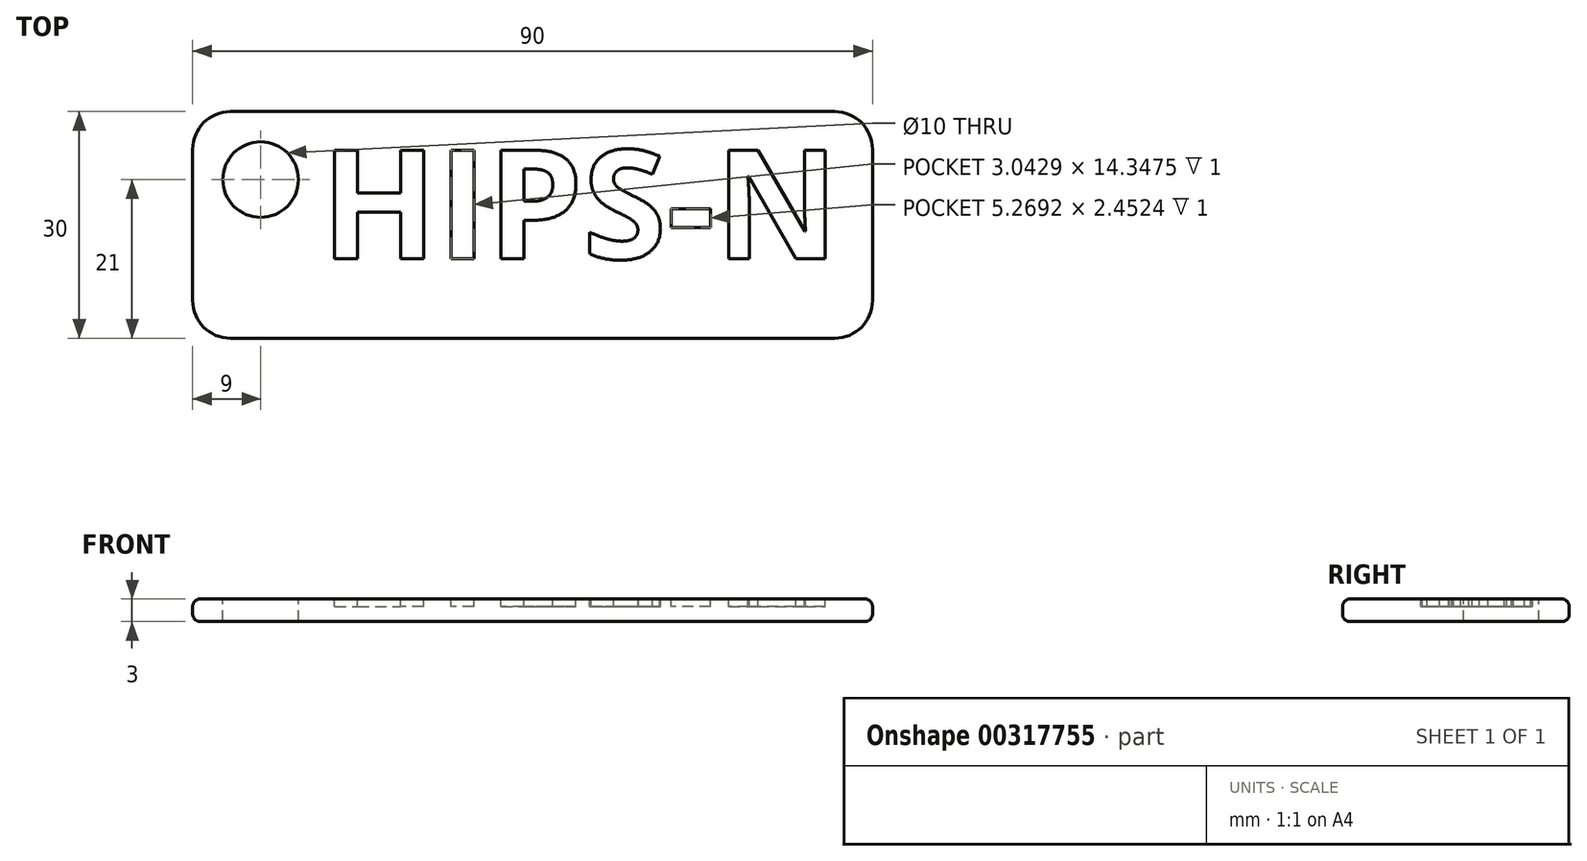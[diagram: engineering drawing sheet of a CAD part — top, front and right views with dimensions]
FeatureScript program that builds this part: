
annotation { "Feature Type Name" : "Feature", "Feature Type Description" : "" }
export const myFeature = defineFeature(function(context is Context, id is Id, definition is map)
    precondition{}
    {
        {
            var Q0;
            Q0=qCreatedBy(makeId("Top.planeOp"),FACE);
            var sketch = newSketch(context, id + "F0", { "sketchPlane" : qUnion([Q0])});
            skLineSegment(sketch, "E0.bottom", {"start": v(-45, 15) * mm, "end": v(45, 15) * mm});
            skLineSegment(sketch, "E0.top", {"start": v(-45, -15) * mm, "end": v(45, -15) * mm});
            skLineSegment(sketch, "E0.left", {"start": v(-45, 15) * mm, "end": v(-45, -15) * mm});
            skLineSegment(sketch, "E0.right", {"start": v(45, 15) * mm, "end": v(45, -15) * mm});
            skLineSegment(sketch, "E1", {"start": v(-45, 15) * mm, "end": v(45, -15) * mm, "construction": true});
            skSolve(sketch);
        }
        {
            var Q0;
            Q0=makeQuery(id+"F0.imprint","IMPRINT",FACE,{"disambiguationData":[TD([[makeQuery(id+"F0.imprint","IMPRINT",EDGE,{"derivedFrom":sQuery(id+"F0.wireOp",EDGE,"E0.bottom")}),-1.0]])]});
            extrude(context, id + "F1", {"entities" : qUnion([Q0]), "depth" : 3 * mm});
        }
        {
            var Q0;
            Q0=makeQuery(id+"F1.opExtrude","CAP_FACE",FACE,{"disambiguationData":[OSD([sQuery(id+"F0.wireOp",EDGE,"E0.bottom"),sQuery(id+"F0.wireOp",EDGE,"E0.top"),sQuery(id+"F0.wireOp",EDGE,"E0.left"),sQuery(id+"F0.wireOp",EDGE,"E0.right")])],"isStart":false});
            var Q1;
            Q1=makeQuery(id+"F1.opExtrude","CAP_FACE",FACE,{"disambiguationData":[OSD([sQuery(id+"F0.wireOp",EDGE,"E0.bottom"),sQuery(id+"F0.wireOp",EDGE,"E0.top"),sQuery(id+"F0.wireOp",EDGE,"E0.left"),sQuery(id+"F0.wireOp",EDGE,"E0.right")])],"isStart":true});
            fillet(context, id + "F2", {"entities" : qUnion([Q0, Q1]), "radius" : 1 * mm, "tangentPropagation" : true, "allowEdgeOverflow" : false});
        }
        {
            var Q0;
            Q0=makeQuery(id+"F1.opExtrude","SWEPT_EDGE",EDGE,{"disambiguationData":[OSD([sQuery(id+"F0.wireOp",EDGE,"E0.top"),sQuery(id+"F0.wireOp",EDGE,"E0.right")])]});
            var Q1;
            Q1=makeQuery(id+"F1.opExtrude","SWEPT_EDGE",EDGE,{"disambiguationData":[OSD([sQuery(id+"F0.wireOp",EDGE,"E0.bottom"),sQuery(id+"F0.wireOp",EDGE,"E0.right")])]});
            var Q2;
            Q2=makeQuery(id+"F1.opExtrude","SWEPT_EDGE",EDGE,{"disambiguationData":[OSD([sQuery(id+"F0.wireOp",EDGE,"E0.bottom"),sQuery(id+"F0.wireOp",EDGE,"E0.left")])]});
            var Q3;
            Q3=makeQuery(id+"F1.opExtrude","SWEPT_EDGE",EDGE,{"disambiguationData":[OSD([sQuery(id+"F0.wireOp",EDGE,"E0.top"),sQuery(id+"F0.wireOp",EDGE,"E0.left")])]});
            fillet(context, id + "F3", {"entities" : qUnion([Q0, Q1, Q2, Q3]), "radius" : 5 * mm, "tangentPropagation" : true, "allowEdgeOverflow" : false});
        }
        {
            var Q0;
            {var subQ0=sQuery(id+"F0.wireOp",EDGE,"E0.left");var subQ2=sQuery(id+"F0.wireOp",EDGE,"E0.bottom");var subQ4=sQuery(id+"F0.wireOp",EDGE,"E0.right");var subQ6=sQuery(id+"F0.wireOp",EDGE,"E0.top");Q0=makeQuery(id+"FmQCBBX3Ub0qneL_1.boolean.opBoolean","SPLIT",FACE,{"disambiguationData":[TD([makeQuery(id+"FmQCBBX3Ub0qneL_1.opExtrude","SWEPT_FACE",FACE,{"disambiguationData":[OSD([sQuery(id+"FOCoeRmDbjhRCuz_1.wireOp",EDGE,"4a1fb44a-e7be-4e23-9449-000d953c446c.sketch_text.stroke-0")])]})])],"derivedFrom":makeQuery(id+"F1.opExtrude","CAP_FACE",FACE,{"disambiguationData":[OSD([subQ2,subQ6,subQ0,subQ4])],"isStart":false})});}
            var sketch = newSketch(context, id + "F4", { "sketchPlane" : qUnion([Q0])});
            skCircle(sketch, "E2", {"center": v(-36, 6) * mm, "radius": 5 * mm});
            skSolve(sketch);
        }
        {
            var Q0;
            Q0=qSketchRegion(id+"F4",true);
            extrude(context, id + "F5", {"entities" : qUnion([Q0]), "operationType" : NewBodyOperationType.REMOVE, "oppositeDirection" : true, "depth" : 3 * mm});
        }
        {
            var Q0;
            Q0=makeQuery(id+"F1.opExtrude","CAP_FACE",FACE,{"disambiguationData":[OSD([sQuery(id+"F0.wireOp",EDGE,"E0.bottom"),sQuery(id+"F0.wireOp",EDGE,"E0.top"),sQuery(id+"F0.wireOp",EDGE,"E0.left"),sQuery(id+"F0.wireOp",EDGE,"E0.right")])],"isStart":false});
            var sketch = newSketch(context, id + "F6", { "sketchPlane" : qUnion([Q0])});
            skText(sketch, "E3", { "text": "HIPS-N", "fontName": "OpenSans-Bold.ttf"});
            const initialGuessF6  = {"E3": [-0.028, -0.00447, 1, 0, 0.01447]};
            skSetInitialGuess(sketch, initialGuessF6);
            skSolve(sketch);
        }
        {
            var Q0;
            Q0=qSketchRegion(id+"F6",true);
            extrude(context, id + "F7", {"entities" : qUnion([Q0]), "operationType" : NewBodyOperationType.REMOVE, "oppositeDirection" : true, "depth" : 1 * mm});
        }
    });
